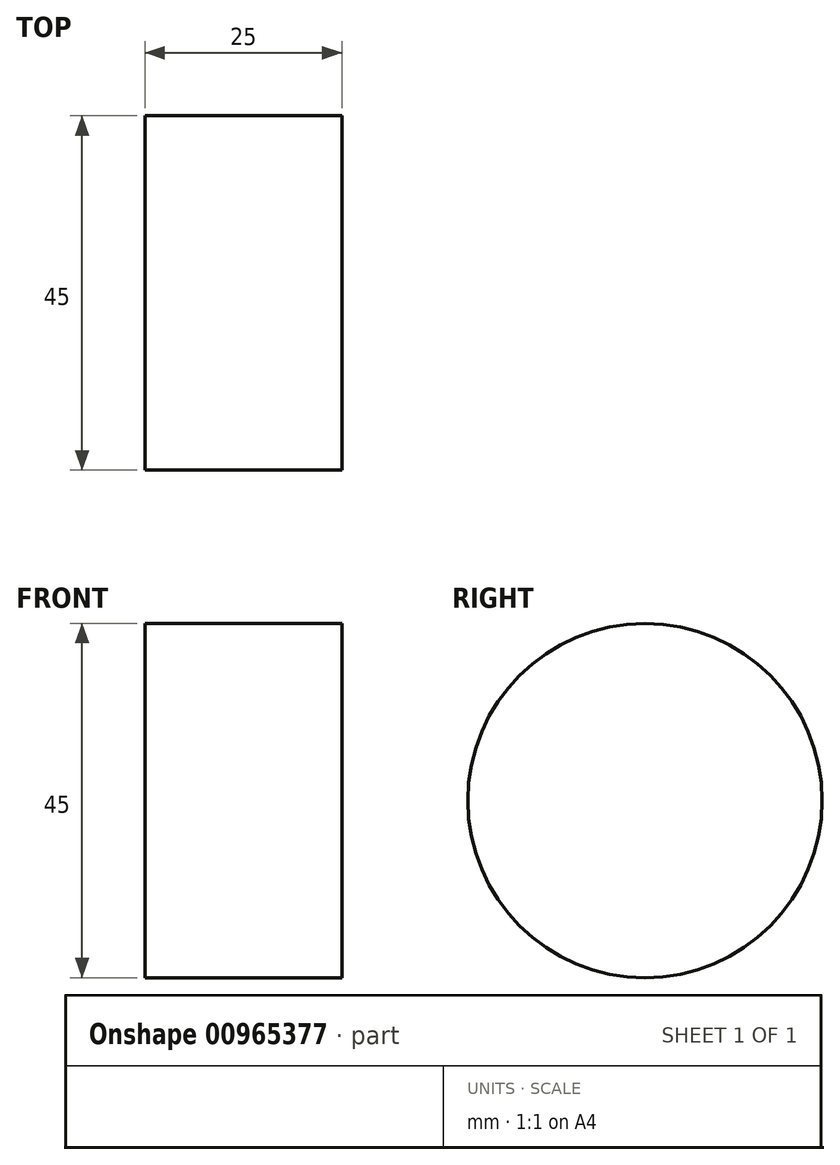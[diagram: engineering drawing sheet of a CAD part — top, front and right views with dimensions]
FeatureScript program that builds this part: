
annotation { "Feature Type Name" : "Feature", "Feature Type Description" : "" }
export const myFeature = defineFeature(function(context is Context, id is Id, definition is map)
    precondition{}
    {
        {
            var Q0;
            Q0=qCreatedBy(makeId("Right.planeOp"),FACE);
            var sketch = newSketch(context, id + "F0", { "sketchPlane" : qUnion([Q0])});
            skCircle(sketch, "E0", {"center": v(0, 0) * mm, "radius": 22.5 * mm});
            skSolve(sketch);
        }
        {
            var Q0;
            Q0 = qSketchRegion(id + "F0", true);
            extrude(context, id + "F1", {"entities" : qUnion([Q0]), "depth" : 25 * mm, "offsetDistance" : 25 * mm});
        }
    });
